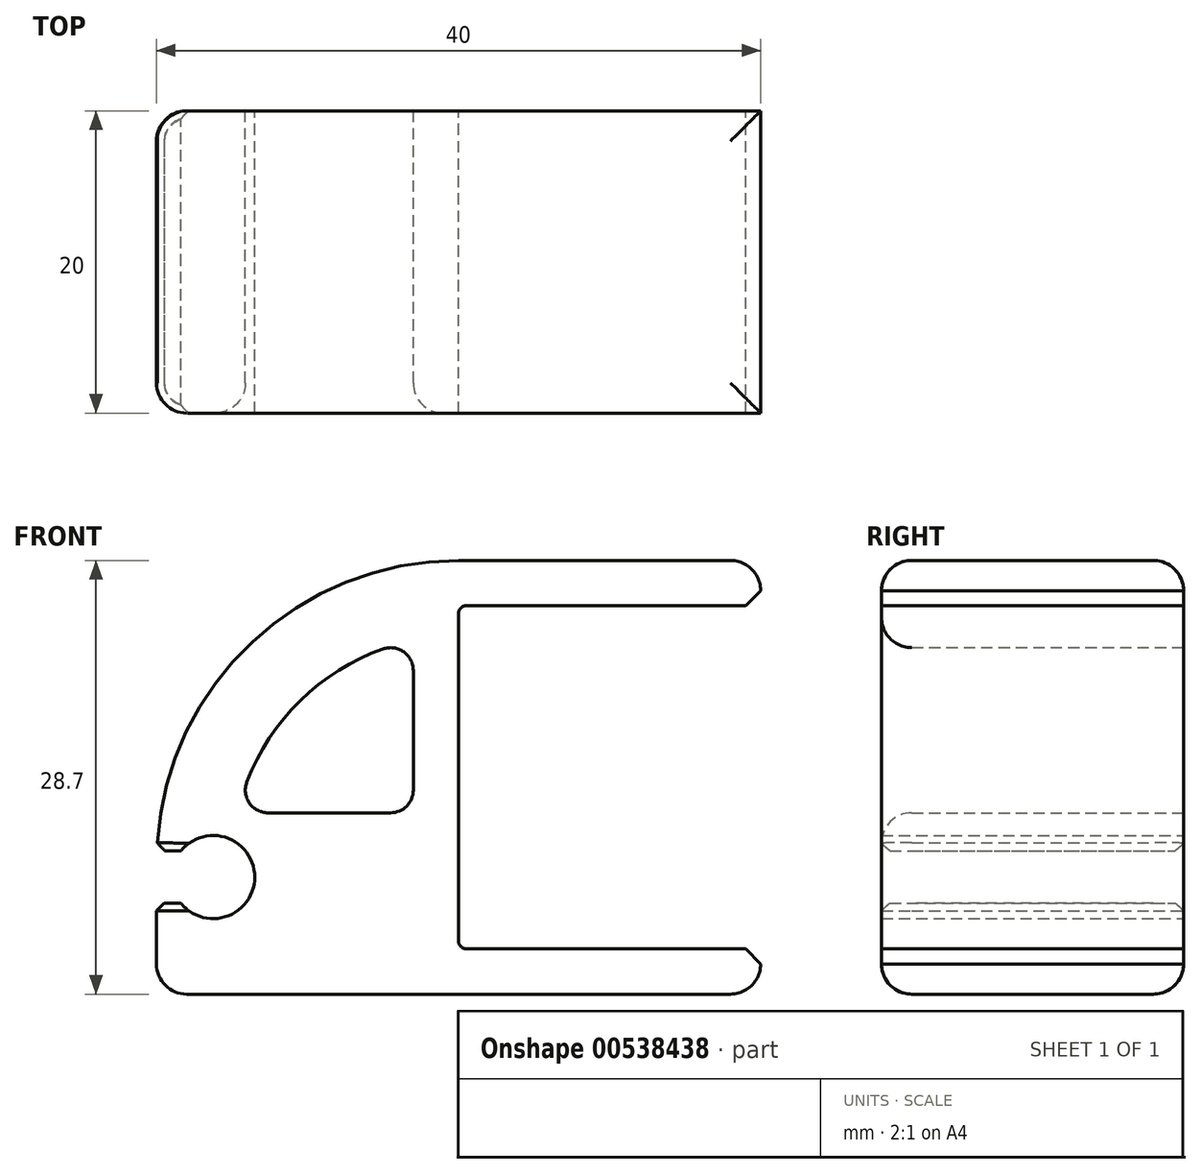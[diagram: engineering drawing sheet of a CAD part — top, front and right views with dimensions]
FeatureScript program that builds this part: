
annotation { "Feature Type Name" : "Feature", "Feature Type Description" : "" }
export const myFeature = defineFeature(function(context is Context, id is Id, definition is map)
    precondition{}
    {
        {
            var Q0;
            Q0=qCreatedBy(makeId("Front.planeOp"),FACE);
            var sketch = newSketch(context, id + "F0", { "sketchPlane" : qUnion([Q0])});
            skLineSegment(sketch, "E0.bottom", {"start": v(0, 0) * mm, "end": v(-40, 0) * mm});
            skLineSegment(sketch, "E0.top", {"start": v(0, 28.7) * mm, "end": v(-20, 28.7) * mm});
            skLineSegment(sketch, "E0.left", {"start": v(0, 0) * mm, "end": v(0, 3) * mm});
            skLineSegment(sketch, "E0.right", {"start": v(-40, 0) * mm, "end": v(-40, 6.01) * mm});
            skLineSegment(sketch, "E1.bottom", {"start": v(0, 25.7) * mm, "end": v(-20, 25.7) * mm});
            skLineSegment(sketch, "E1.top", {"start": v(0, 3) * mm, "end": v(-20, 3) * mm});
            skLineSegment(sketch, "E1.right", {"start": v(-20, 25.7) * mm, "end": v(-20, 3) * mm});
            skLineSegment(sketch, "E2.trimOffspring", {"start": v(0, 25.7) * mm, "end": v(0, 28.7) * mm});
            skArc(sketch, "E3", {"start": v(-38.38, 6.01) * mm, "mid": v(-33.5, 7.75) * mm, "end": v(-38.38, 9.49) * mm});
            skLineSegment(sketch, "E4.bottom", {"start": v(-40.08, 9.49) * mm, "end": v(-38.38, 9.49) * mm});
            skPoint(sketch, "E4.right.start.orphan", {"position": v(-40.08, 9.49) * mm});
            skPoint(sketch, "E5.orphan", {"position": v(-21.67, 6.01) * mm});
            skLineSegment(sketch, "E6", {"start": v(-38.38, 6.01) * mm, "end": v(-40, 6.01) * mm});
            skPoint(sketch, "E4.top.start.orphan", {"position": v(-32.42, 6.01) * mm});
            skPoint(sketch, "E7.orphan", {"position": v(-50.83, 9.49) * mm});
            skPoint(sketch, "E8.visualSharp", {"position": v(-40, 28.7) * mm});
            skArc(sketch, "E8.filletArc", {"start": v(-20, 28.7) * mm, "mid": v(-33.86, 23.12) * mm, "end": v(-39.98, 9.49) * mm});
            skLineSegment(sketch, "E9", {"start": v(-39.98, 9.49) * mm, "end": v(-40.08, 9.49) * mm});
            skSolve(sketch);
        }
        {
            var Q0;
            Q0=makeQuery(id+"F0.imprint","IMPRINT",FACE,{"disambiguationData":[TD([[makeQuery(id+"F0.imprint","IMPRINT",EDGE,{"derivedFrom":sQuery(id+"F0.wireOp",EDGE,"E0.bottom")}),-1.0]])]});
            extrude(context, id + "F1", {"entities" : qUnion([Q0]), "depth" : 20 * mm, "offsetDistance" : 25 * mm});
        }
        {
            var Q0;
            Q0=makeQuery(id+"F1.opExtrude","SWEPT_EDGE",EDGE,{"disambiguationData":[OSD([sQuery(id+"F0.wireOp",EDGE,"E1.bottom"),sQuery(id+"F0.wireOp",EDGE,"E2.trimOffspring")])]});
            var Q1;
            Q1=makeQuery(id+"F1.opExtrude","SWEPT_EDGE",EDGE,{"disambiguationData":[OSD([sQuery(id+"F0.wireOp",EDGE,"E0.left"),sQuery(id+"F0.wireOp",EDGE,"E1.top")])]});
            chamfer(context, id + "F2", {"entities" : qUnion([Q0, Q1]), "width" : 1 * mm, "tangentPropagation" : true});
        }
        {
            var Q0;
            Q0=makeQuery(id+"F1.opExtrude","CAP_EDGE",EDGE,{"disambiguationData":[OSD([sQuery(id+"F0.wireOp",EDGE,"E8.filletArc")])],"isStart":true});
            var Q1;
            Q1=makeQuery(id+"F1.opExtrude","CAP_EDGE",EDGE,{"disambiguationData":[OSD([sQuery(id+"F0.wireOp",EDGE,"E8.filletArc")])],"isStart":false});
            var Q2;
            Q2=makeQuery(id+"F1.opExtrude","CAP_EDGE",EDGE,{"disambiguationData":[OSD([sQuery(id+"F0.wireOp",EDGE,"E0.right")])],"isStart":false});
            var Q3;
            Q3=makeQuery(id+"F1.opExtrude","CAP_EDGE",EDGE,{"disambiguationData":[OSD([sQuery(id+"F0.wireOp",EDGE,"E0.right")])],"isStart":true});
            var Q4;
            Q4=makeQuery(id+"F1.opExtrude","SWEPT_EDGE",EDGE,{"disambiguationData":[OSD([sQuery(id+"F0.wireOp",EDGE,"E0.top"),sQuery(id+"F0.wireOp",EDGE,"E2.trimOffspring")])]});
            var Q5;
            Q5=makeQuery(id+"F1.opExtrude","SWEPT_EDGE",EDGE,{"disambiguationData":[OSD([sQuery(id+"F0.wireOp",EDGE,"E0.bottom"),sQuery(id+"F0.wireOp",EDGE,"E0.left")])]});
            var Q6;
            Q6=makeQuery(id+"F1.opExtrude","CAP_EDGE",EDGE,{"disambiguationData":[OSD([sQuery(id+"F0.wireOp",EDGE,"E0.bottom")])],"isStart":true});
            var Q7;
            Q7=makeQuery(id+"F1.opExtrude","CAP_EDGE",EDGE,{"disambiguationData":[OSD([sQuery(id+"F0.wireOp",EDGE,"E0.bottom")])],"isStart":false});
            var Q8;
            Q8=makeQuery(id+"F1.opExtrude","SWEPT_EDGE",EDGE,{"disambiguationData":[OSD([sQuery(id+"F0.wireOp",EDGE,"E0.bottom"),sQuery(id+"F0.wireOp",EDGE,"E0.right")])]});
            fillet(context, id + "F3", {"entities" : qUnion([Q0, Q1, Q2, Q3, Q4, Q5, Q6, Q7, Q8]), "radius" : 2 * mm, "tangentPropagation" : true, "allowEdgeOverflow" : false});
        }
        {
            var Q0;
            Q0=makeQuery(id+"F1.opExtrude","SWEPT_EDGE",EDGE,{"disambiguationData":[OSD([sQuery(id+"F0.wireOp",EDGE,"E0.right"),sQuery(id+"F0.wireOp",EDGE,"E6")])]});
            var Q1;
            Q1=makeQuery(id+"F1.opExtrude","SWEPT_EDGE",EDGE,{"disambiguationData":[OSD([sQuery(id+"F0.wireOp",EDGE,"E8.filletArc"),sQuery(id+"F0.wireOp",EDGE,"E9")])]});
            chamfer(context, id + "F4", {"entities" : qUnion([Q0, Q1]), "width" : .5 * mm, "tangentPropagation" : true});
        }
        {
            var Q0;
            Q0=makeQuery(id+"F1.opExtrude","CAP_FACE",FACE,{"disambiguationData":[OSD([sQuery(id+"F0.wireOp",EDGE,"E0.bottom"),sQuery(id+"F0.wireOp",EDGE,"E0.top"),sQuery(id+"F0.wireOp",EDGE,"E0.left"),sQuery(id+"F0.wireOp",EDGE,"E0.right"),sQuery(id+"F0.wireOp",EDGE,"E1.bottom"),sQuery(id+"F0.wireOp",EDGE,"E1.top"),sQuery(id+"F0.wireOp",EDGE,"E1.right"),sQuery(id+"F0.wireOp",EDGE,"E2.trimOffspring"),sQuery(id+"F0.wireOp",EDGE,"E3"),sQuery(id+"F0.wireOp",EDGE,"E4.bottom"),sQuery(id+"F0.wireOp",EDGE,"E6"),sQuery(id+"F0.wireOp",EDGE,"E8.filletArc"),sQuery(id+"F0.wireOp",EDGE,"E9")])],"isStart":true});
            var sketch = newSketch(context, id + "F5", { "sketchPlane" : qUnion([Q0])});
            skArc(sketch, "E10.0", {"start": v(34.02, 14.03) * mm, "mid": v(30.48, 19.43) * mm, "end": v(25, 22.84) * mm});
            skLineSegment(sketch, "E11.0", {"start": v(23, 21.43) * mm, "end": v(23, 13.5) * mm});
            skLineSegment(sketch, "E12.0", {"start": v(24.5, 12) * mm, "end": v(32.62, 12) * mm});
            skPoint(sketch, "E13.visualSharp", {"position": v(23, 23.4) * mm});
            skArc(sketch, "E13.filletArc", {"start": v(25, 22.84) * mm, "mid": v(23.63, 22.65) * mm, "end": v(23, 21.43) * mm});
            skPoint(sketch, "E14.visualSharp", {"position": v(23, 12) * mm});
            skArc(sketch, "E14.filletArc", {"start": v(23, 13.5) * mm, "mid": v(23.44, 12.44) * mm, "end": v(24.5, 12) * mm});
            skPoint(sketch, "E15.visualSharp", {"position": v(34.63, 12) * mm});
            skArc(sketch, "E15.filletArc", {"start": v(32.62, 12) * mm, "mid": v(33.85, 12.65) * mm, "end": v(34.02, 14.03) * mm});
            skSolve(sketch);
        }
        {
            var Q0;
            Q0=makeQuery(id+"F5.imprint","IMPRINT",FACE,{"disambiguationData":[TD([[makeQuery(id+"F5.imprint","IMPRINT",EDGE,{"derivedFrom":sQuery(id+"F5.wireOp",EDGE,"E10.0")}),1.0]])]});
            extrude(context, id + "F6", {"entities" : qUnion([Q0]), "operationType" : NewBodyOperationType.REMOVE, "endBound" : BoundingType.THROUGH_ALL, "oppositeDirection" : true, "depth" : 25 * mm, "offsetDistance" : 25 * mm});
        }
        {
            var Q0;
            Q0=makeQuery(id+"F6.boolean.opBoolean","COPY",EDGE,{"derivedFrom":makeQuery(id+"F6.opExtrude","CAP_EDGE",EDGE,{"disambiguationData":[OSD([sQuery(id+"F5.wireOp",EDGE,"E10.0")])],"isStart":true})});
            var Q1;
            Q1=makeQuery(id+"F6.boolean.opBoolean","INTERSECT",EDGE,{"derivedFrom":[makeQuery(id+"F1.opExtrude","CAP_FACE",FACE,{"disambiguationData":[OSD([sQuery(id+"F0.wireOp",EDGE,"E0.bottom"),sQuery(id+"F0.wireOp",EDGE,"E0.top"),sQuery(id+"F0.wireOp",EDGE,"E0.left"),sQuery(id+"F0.wireOp",EDGE,"E0.right"),sQuery(id+"F0.wireOp",EDGE,"E1.bottom"),sQuery(id+"F0.wireOp",EDGE,"E1.top"),sQuery(id+"F0.wireOp",EDGE,"E1.right"),sQuery(id+"F0.wireOp",EDGE,"E2.trimOffspring"),sQuery(id+"F0.wireOp",EDGE,"E3"),sQuery(id+"F0.wireOp",EDGE,"E4.bottom"),sQuery(id+"F0.wireOp",EDGE,"E6"),sQuery(id+"F0.wireOp",EDGE,"E8.filletArc"),sQuery(id+"F0.wireOp",EDGE,"E9")])],"isStart":false}),makeQuery(id+"F6.opExtrude","SWEPT_FACE",FACE,{"disambiguationData":[OSD([sQuery(id+"F5.wireOp",EDGE,"E10.0")])]})]});
            fillet(context, id + "F7", {"entities" : qUnion([Q0, Q1]), "radius" : 2 * mm, "tangentPropagation" : true, "allowEdgeOverflow" : false});
        }
        {
            var Q0;
            Q0=makeQuery(id+"F1.opExtrude","SWEPT_EDGE",EDGE,{"disambiguationData":[OSD([sQuery(id+"F0.wireOp",EDGE,"E1.bottom"),sQuery(id+"F0.wireOp",EDGE,"E1.right")])]});
            var Q1;
            Q1=makeQuery(id+"F1.opExtrude","SWEPT_EDGE",EDGE,{"disambiguationData":[OSD([sQuery(id+"F0.wireOp",EDGE,"E1.top"),sQuery(id+"F0.wireOp",EDGE,"E1.right")])]});
            fillet(context, id + "F8", {"entities" : qUnion([Q0, Q1]), "radius" : .5 * mm, "tangentPropagation" : true, "allowEdgeOverflow" : false});
        }
    });
